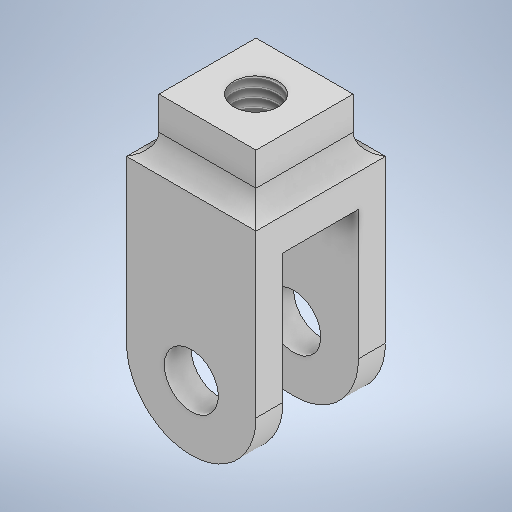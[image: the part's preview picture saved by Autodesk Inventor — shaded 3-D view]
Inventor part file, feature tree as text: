
AUTODESK INVENTOR PART (.ipt)
format: ipt  version: 2025 (Build 290162010, 162A)  size: 296,960 bytes
history: native  units: mm
features: sketch x6, extrude x4, hole x2, fillet x1, projected_geometry x1
ambient origin geometry x8: Origin, YZ Plane, XZ Plane, XY Plane, X Axis, Y Axis, Z Axis, Center Point
bodies: Solid1 (feature_tree)
feature tree (14):
  extrude  "Extrusion1"  Depth=15.0mm
  extrude  "Extrusion2"  Depth=12.0mm TaperAngle=0.0deg
  extrude  "Extrusion3"  Depth=7.0mm
  hole  "Hole1"  [1 undecoded]
  extrude  "Extrusion4"  Depth=2.0mm TaperAngle=0.0deg
  fillet  "Fillet1"  Radius=2.0mm
  hole  "Hole2"  [1 undecoded]
  sketch  "Sketch1"  dims[d0=12.0mm d1=15.0mm]
  sketch  "Sketch4"  dims[d2=12.0mm d3=0.0mm d6=12.0mm d7=0.0mm]
  sketch  "Sketch5"  dims[d8=18.0mm d9=7.0mm]
  projected_geometry  "Projected Loop2"
  sketch  "Sketch6"  dims[d10=10.0mm d11=0.0mm]
  sketch  "Sketch7"  dims[d12=5.0mm d13=6.0mm d14=4.0mm d15=2.0mm d16=90.0deg d17=8.0mm d18=0.0mm d19=9.0mm]
  sketch  "Sketch8"  dims[d20=9.0mm d21=5.0mm d22=0.0mm d23=2.0mm d24=4.134mm d25=10.0mm d26=4.0mm d27=2.0mm d28=90.0deg d29=8.0mm d30=0.0mm]
note: 2 required parameter values undecoded (feature->parameter linkage not recoverable at this tier; creation-order binding heuristic only, values carry confidence <= 0.55)
